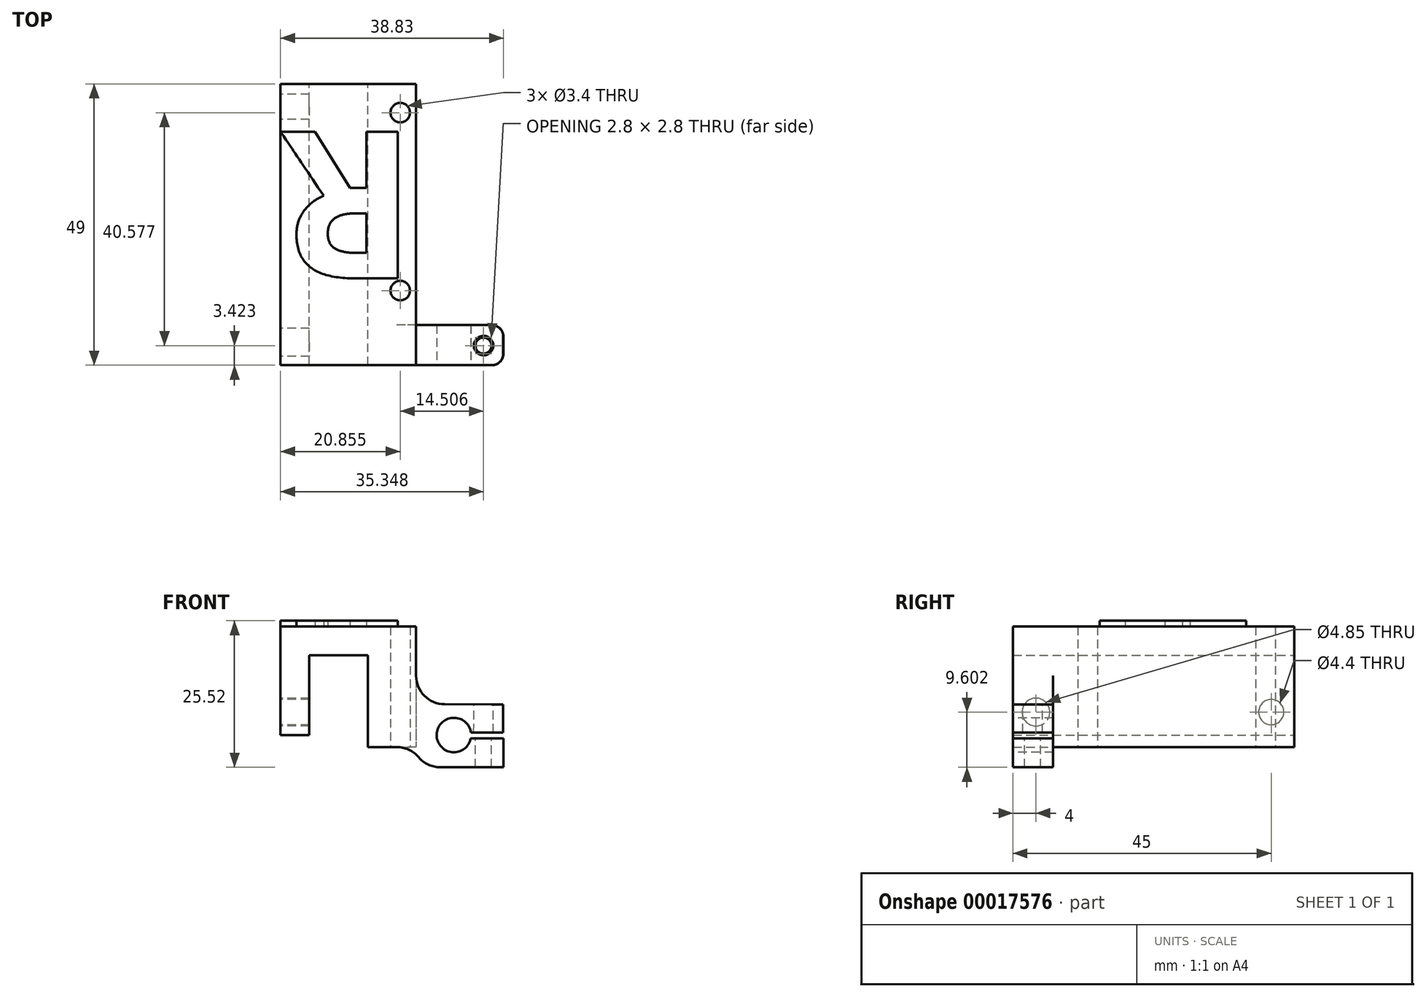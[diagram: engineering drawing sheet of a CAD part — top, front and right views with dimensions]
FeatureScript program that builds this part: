
annotation { "Feature Type Name" : "Feature", "Feature Type Description" : "" }
export const myFeature = defineFeature(function(context is Context, id is Id, definition is map)
    precondition{}
    {
        {
            var Q0;
            Q0=qCreatedBy(makeId("Front.planeOp"),FACE);
            var sketch = newSketch(context, id + "F0", { "sketchPlane" : qUnion([Q0])});
            skLineSegment(sketch, "E0", {"start": v(-18.67, 10.9) * mm, "end": v(-18.67, 29.8) * mm});
            skLineSegment(sketch, "E1", {"start": v(-18.67, 29.8) * mm, "end": v(4.94, 29.8) * mm});
            skLineSegment(sketch, "E2", {"start": v(4.94, 29.8) * mm, "end": v(4.94, 16.27) * mm});
            skLineSegment(sketch, "E3", {"start": v(-3.47, 8.8) * mm, "end": v(-3.47, 24.8) * mm});
            skLineSegment(sketch, "E4", {"start": v(-3.47, 24.8) * mm, "end": v(-13.67, 24.8) * mm});
            skLineSegment(sketch, "E5", {"start": v(-13.67, 24.8) * mm, "end": v(-13.67, 10.9) * mm});
            skLineSegment(sketch, "E6", {"start": v(-13.67, 10.9) * mm, "end": v(-18.67, 10.9) * mm});
            skLineSegment(sketch, "E7", {"start": v(4.94, 16.27) * mm, "end": v(4.94, 8.8) * mm});
            skLineSegment(sketch, "E8", {"start": v(4.94, 8.8) * mm, "end": v(-3.47, 8.8) * mm});
            skLineSegment(sketch, "E9", {"start": v(4.94, 16.27) * mm, "end": v(4.94, 16.27) * mm});
            skLineSegment(sketch, "E10", {"start": v(20.13, 16.24) * mm, "end": v(20.13, 11.34) * mm});
            skLineSegment(sketch, "E11", {"start": v(20.13, 11.34) * mm, "end": v(13.49, 11.34) * mm});
            skLineSegment(sketch, "E12", {"start": v(13.49, 11.34) * mm, "end": v(13.49, 10.34) * mm});
            skLineSegment(sketch, "E13", {"start": v(13.49, 10.34) * mm, "end": v(20.16, 10.34) * mm});
            skLineSegment(sketch, "E14", {"start": v(20.16, 10.34) * mm, "end": v(20.16, 5.29) * mm});
            skLineSegment(sketch, "E15", {"start": v(20.16, 5.29) * mm, "end": v(6.35, 5.29) * mm});
            skLineSegment(sketch, "E16", {"start": v(6.35, 5.29) * mm, "end": v(4.94, 8.8) * mm});
            skLineSegment(sketch, "E17", {"start": v(20.13, 16.24) * mm, "end": v(4.94, 16.27) * mm});
            skSolve(sketch);
        }
        {
            var Q0;
            Q0=makeQuery(id+"F0.imprint","IMPRINT",FACE,{"disambiguationData":[TD([[makeQuery(id+"F0.imprint","IMPRINT",EDGE,{"derivedFrom":sQuery(id+"F0.wireOp",EDGE,"E0")}),-1.0]])]});
            var Q1;
            {var subQ2=sQuery(id+"F0.wireOp",EDGE,"69cbcc5d-e0c3-48db-8baf-3487a8abab7d");Q1=makeQuery(id+"F0.imprint","IMPRINT",FACE,{"disambiguationData":[TD([[makeQuery(id+"F0.imprint","IMPRINT",EDGE,{"derivedFrom":subQ2}),-1.0]])]});}
            var Q2;
            Q2=makeQuery(id+"F0.imprint","IMPRINT",FACE,{"disambiguationData":[TD([[makeQuery(id+"F0.imprint","IMPRINT",EDGE,{"derivedFrom":sQuery(id+"F0.wireOp",EDGE,"E7")}),1.0]])]});
            extrude(context, id + "F1", {"entities" : qUnion([Q0, Q1, Q2]), "depth" : 7 * mm});
        }
        {
            var Q0;
            Q0=makeQuery(id+"F0.imprint","IMPRINT",FACE,{"disambiguationData":[TD([[makeQuery(id+"F0.imprint","IMPRINT",EDGE,{"derivedFrom":sQuery(id+"F0.wireOp",EDGE,"E0")}),-1.0]])]});
            extrude(context, id + "F2", {"entities" : qUnion([Q0]), "operationType" : NewBodyOperationType.ADD, "oppositeDirection" : true, "depth" : 42 * mm});
        }
        {
            var Q0;
            {var subQ0=sQuery(id+"F0.wireOp",EDGE,"E8");Q0=makeQuery(id+"F2.boolean.opBoolean","MERGE",FACE,{"derivedFrom":[makeQuery(id+"F1.opExtrude","SWEPT_FACE",FACE,{"disambiguationData":[OSD([subQ0])]}),makeQuery(id+"F2.opExtrude","SWEPT_FACE",FACE,{"disambiguationData":[OSD([subQ0])]})]});}
            var sketch = newSketch(context, id + "F3", { "sketchPlane" : qUnion([Q0])});
            skCircle(sketch, "E18", {"center": v(2.19, -6) * mm, "radius": 1.7 * mm});
            skCircle(sketch, "E19", {"center": v(2.19, -37) * mm, "radius": 1.7 * mm});
            skCircle(sketch, "E20", {"center": v(17.69, -21.5) * mm, "radius": 11 * mm});
            skSolve(sketch);
        }
        {
            var Q0;
            Q0=qSketchRegion(id+"F3",true);
            extrude(context, id + "F4", {"entities" : qUnion([Q0]), "operationType" : NewBodyOperationType.REMOVE, "endBound" : BoundingType.THROUGH_ALL, "oppositeDirection" : true, "depth" : 25 * mm});
        }
        {
            var Q0;
            Q0=makeQuery(id+"F1.opExtrude","CAP_FACE",FACE,{"disambiguationData":[OSD([sQuery(id+"F0.wireOp",EDGE,"E0"),sQuery(id+"F0.wireOp",EDGE,"E1"),sQuery(id+"F0.wireOp",EDGE,"E2"),sQuery(id+"F0.wireOp",EDGE,"E3"),sQuery(id+"F0.wireOp",EDGE,"E4"),sQuery(id+"F0.wireOp",EDGE,"E5"),sQuery(id+"F0.wireOp",EDGE,"E6"),sQuery(id+"F0.wireOp",EDGE,"E8"),sQuery(id+"F0.wireOp",EDGE,"E9"),sQuery(id+"F0.wireOp",EDGE,"58f11638-63e7-4b32-8aff-a1ba3c53649b"),sQuery(id+"F0.wireOp",EDGE,"E10"),sQuery(id+"F0.wireOp",EDGE,"E11"),sQuery(id+"F0.wireOp",EDGE,"E12"),sQuery(id+"F0.wireOp",EDGE,"E13"),sQuery(id+"F0.wireOp",EDGE,"E14"),sQuery(id+"F0.wireOp",EDGE,"E15"),sQuery(id+"F0.wireOp",EDGE,"E16")])],"isStart":false});
            var sketch = newSketch(context, id + "F5", { "sketchPlane" : qUnion([Q0])});
            skCircle(sketch, "E21", {"center": v(11.53, 10.9) * mm, "radius": 3 * mm});
            skSolve(sketch);
        }
        {
            var Q0;
            Q0=qSketchRegion(id+"F5",true);
            extrude(context, id + "F6", {"entities" : qUnion([Q0]), "operationType" : NewBodyOperationType.REMOVE, "oppositeDirection" : true, "depth" : 10 * mm});
        }
        {
            var Q0;
            Q0=qSketchRegion(id+"F3",true);
            extrude(context, id + "F7", {"entities" : qUnion([Q0]), "operationType" : NewBodyOperationType.REMOVE, "endBound" : BoundingType.THROUGH_ALL, "oppositeDirection" : true, "depth" : 25 * mm});
        }
        {
            var Q0;
            Q0=makeQuery(id+"F1.opExtrude","SWEPT_FACE",FACE,{"disambiguationData":[OSD([sQuery(id+"F0.wireOp",EDGE,"E17")])]});
            var sketch = newSketch(context, id + "F8", { "sketchPlane" : qUnion([Q0])});
            skCircle(sketch, "E22", {"center": v(16.67, -3.58) * mm, "radius": 1.7 * mm});
            skCircle(sketch, "E23", {"center": v(16.67, -3.58) * mm, "radius": 1.4 * mm});
            skSolve(sketch);
        }
        {
            var Q0;
            Q0=makeQuery(id+"F8.imprint","IMPRINT",FACE,{"disambiguationData":[TD([[makeQuery(id+"F8.imprint","IMPRINT",EDGE,{"derivedFrom":sQuery(id+"F8.wireOp",EDGE,"E23")}),1.0]])]});
            extrude(context, id + "F9", {"entities" : qUnion([Q0]), "operationType" : NewBodyOperationType.REMOVE, "endBound" : BoundingType.THROUGH_ALL, "oppositeDirection" : true, "depth" : 25 * mm});
        }
        {
            var Q0;
            Q0=makeQuery(id+"F8.imprint","IMPRINT",FACE,{"disambiguationData":[TD([[makeQuery(id+"F8.imprint","IMPRINT",EDGE,{"derivedFrom":sQuery(id+"F8.wireOp",EDGE,"E22")}),1.0]])]});
            extrude(context, id + "F10", {"entities" : qUnion([Q0]), "operationType" : NewBodyOperationType.REMOVE, "endBound" : BoundingType.UP_TO_NEXT, "oppositeDirection" : true, "depth" : 25 * mm});
        }
        {
            var Q0;
            Q0=makeQuery(id+"F1.opExtrude","SWEPT_EDGE",EDGE,{"disambiguationData":[OSD([sQuery(id+"F0.wireOp",EDGE,"E2"),sQuery(id+"F0.wireOp",EDGE,"E7"),sQuery(id+"F0.wireOp",EDGE,"E17")])]});
            fillet(context, id + "F11", {"entities" : qUnion([Q0]), "radius" : 5 * mm, "tangentPropagation" : true, "allowEdgeOverflow" : false});
        }
        {
            var Q0;
            Q0=makeQuery(id+"F1.opExtrude","SWEPT_EDGE",EDGE,{"disambiguationData":[OSD([sQuery(id+"F0.wireOp",EDGE,"E7"),sQuery(id+"F0.wireOp",EDGE,"E8"),sQuery(id+"F0.wireOp",EDGE,"E16")])]});
            fillet(context, id + "F12", {"entities" : qUnion([Q0]), "radius" : 5 * mm, "tangentPropagation" : true, "allowEdgeOverflow" : false});
        }
        {
            var Q0;
            Q0=makeQuery(id+"F1.opExtrude","SWEPT_EDGE",EDGE,{"disambiguationData":[OSD([sQuery(id+"F0.wireOp",EDGE,"E15"),sQuery(id+"F0.wireOp",EDGE,"E16")])]});
            fillet(context, id + "F13", {"entities" : qUnion([Q0]), "radius" : 5 * mm, "tangentPropagation" : true, "allowEdgeOverflow" : false});
        }
        {
            var Q0;
            Q0=makeQuery(id+"F1.opExtrude","CAP_EDGE",EDGE,{"disambiguationData":[OSD([sQuery(id+"F0.wireOp",EDGE,"E10")])],"isStart":false});
            var Q1;
            Q1=makeQuery(id+"F1.opExtrude","CAP_EDGE",EDGE,{"disambiguationData":[OSD([sQuery(id+"F0.wireOp",EDGE,"E14")])],"isStart":false});
            var Q2;
            Q2=makeQuery(id+"F1.opExtrude","CAP_EDGE",EDGE,{"disambiguationData":[OSD([sQuery(id+"F0.wireOp",EDGE,"E10")])],"isStart":true});
            var Q3;
            Q3=makeQuery(id+"F1.opExtrude","CAP_EDGE",EDGE,{"disambiguationData":[OSD([sQuery(id+"F0.wireOp",EDGE,"E14")])],"isStart":true});
            fillet(context, id + "F14", {"entities" : qUnion([Q0, Q1, Q2, Q3]), "radius" : 2 * mm, "tangentPropagation" : true, "allowEdgeOverflow" : false});
        }
        {
            var Q0;
            {var subQ0=sQuery(id+"F0.wireOp",EDGE,"E0");Q0=makeQuery(id+"F2.boolean.opBoolean","MERGE",FACE,{"derivedFrom":[makeQuery(id+"F1.opExtrude","SWEPT_FACE",FACE,{"disambiguationData":[OSD([subQ0])]}),makeQuery(id+"F2.opExtrude","SWEPT_FACE",FACE,{"disambiguationData":[OSD([subQ0])]})]});}
            var sketch = newSketch(context, id + "F15", { "sketchPlane" : qUnion([Q0])});
            skCircle(sketch, "E24", {"center": v(-38, 14.9) * mm, "radius": 2.2 * mm});
            skCircle(sketch, "E25", {"center": v(3, 14.9) * mm, "radius": 2.43 * mm});
            skSolve(sketch);
        }
        {
            var Q0;
            Q0=qSketchRegion(id+"F15",true);
            extrude(context, id + "F16", {"entities" : qUnion([Q0]), "operationType" : NewBodyOperationType.REMOVE, "oppositeDirection" : true, "depth" : 6 * mm});
        }
        {
            var Q0;
            {var subQ0=sQuery(id+"F0.wireOp",EDGE,"E1");Q0=makeQuery(id+"F2.boolean.opBoolean","MERGE",FACE,{"derivedFrom":[makeQuery(id+"F1.opExtrude","SWEPT_FACE",FACE,{"disambiguationData":[OSD([subQ0])]}),makeQuery(id+"F2.opExtrude","SWEPT_FACE",FACE,{"disambiguationData":[OSD([subQ0])]})]});}
            var sketch = newSketch(context, id + "F17", { "sketchPlane" : qUnion([Q0])});
            skText(sketch, "E26", { "text": "R", "fontName": "OpenSans-Bold.ttf"});
            const initialGuessF17  = {"E26": [0.00494, 0.03366, -1, 0, 0.02575]};
            skSetInitialGuess(sketch, initialGuessF17);
            skSolve(sketch);
        }
        {
            var Q0;
            Q0=qSketchRegion(id+"F17",true);
            extrude(context, id + "F18", {"entities" : qUnion([Q0]), "operationType" : NewBodyOperationType.ADD, "depth" : 1 * mm});
        }
    });
